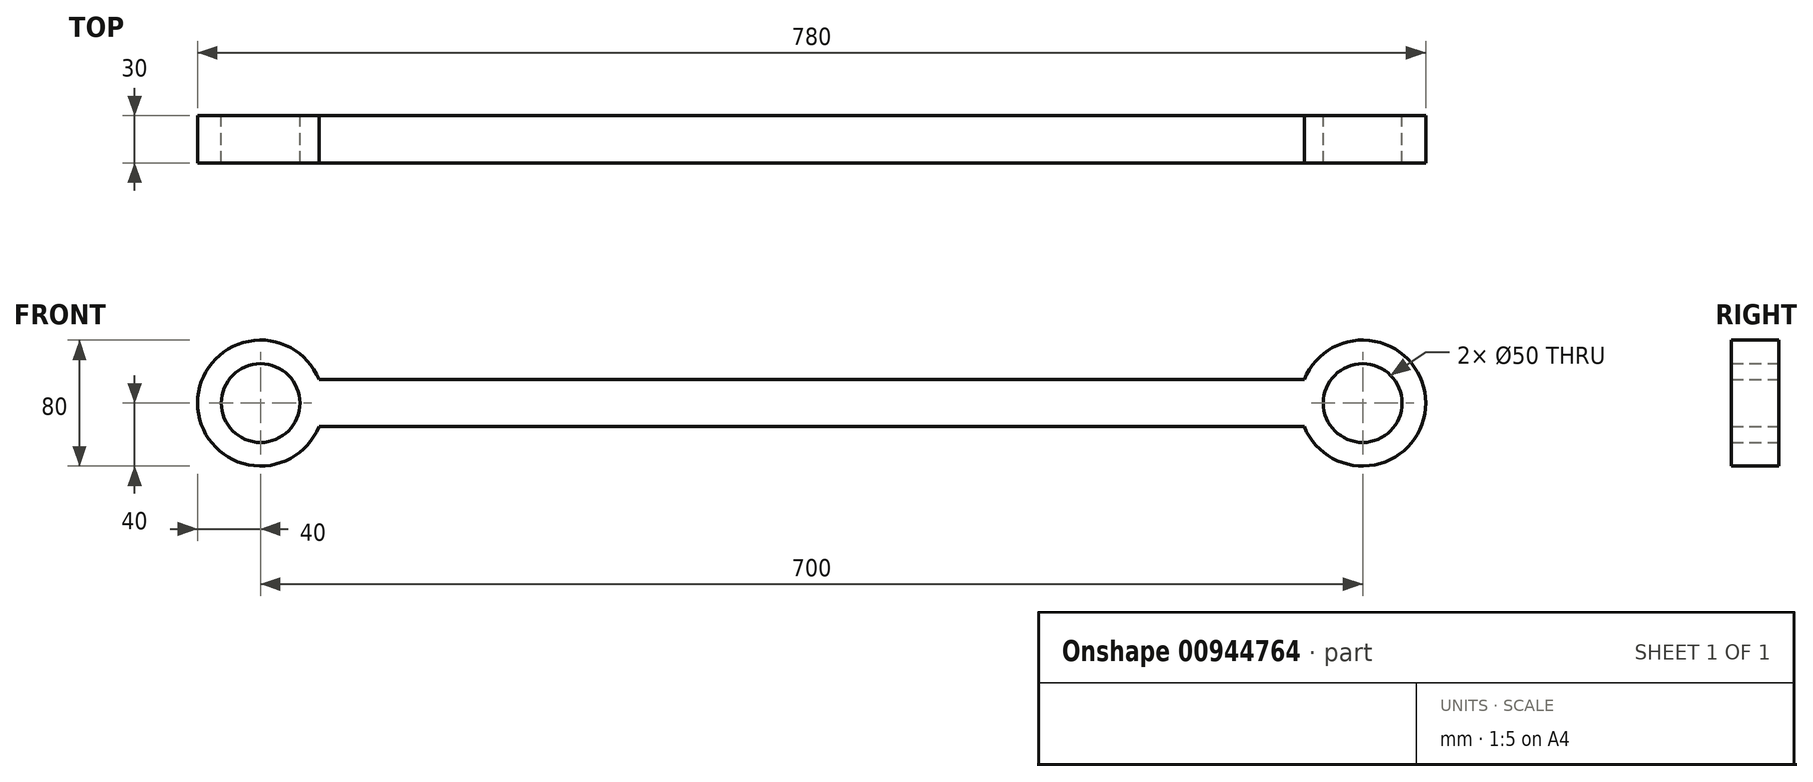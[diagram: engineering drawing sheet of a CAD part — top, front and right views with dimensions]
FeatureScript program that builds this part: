
annotation { "Feature Type Name" : "Feature", "Feature Type Description" : "" }
export const myFeature = defineFeature(function(context is Context, id is Id, definition is map)
    precondition{}
    {
        {
            var Q0;
            Q0=qCreatedBy(makeId("Front.planeOp"),FACE);
            var sketch = newSketch(context, id + "F0", { "sketchPlane" : qUnion([Q0])});
            skCircle(sketch, "E0", {"center": v(-350, 0) * mm, "radius": 25 * mm});
            skCircle(sketch, "E1", {"center": v(350, 0) * mm, "radius": 25 * mm});
            skArc(sketch, "E2", {"start": v(-312.92, 15) * mm, "mid": v(-390, 0) * mm, "end": v(-312.92, -15) * mm});
            skArc(sketch, "E3", {"start": v(312.92, -15) * mm, "mid": v(390, 0) * mm, "end": v(312.92, 15) * mm});
            skLineSegment(sketch, "E4.bottom", {"start": v(312.92, -15) * mm, "end": v(-312.92, -15) * mm});
            skLineSegment(sketch, "E4.top", {"start": v(312.92, 15) * mm, "end": v(-312.92, 15) * mm});
            skLineSegment(sketch, "E4.left", {"start": v(312.92, -15) * mm, "end": v(312.92, 15) * mm, "construction": true});
            skLineSegment(sketch, "E4.right", {"start": v(-312.92, -15) * mm, "end": v(-312.92, 15) * mm, "construction": true});
            skPoint(sketch, "E4.middle", {"position": v(0, 0) * mm});
            skLineSegment(sketch, "E5", {"start": v(-250.43, 0) * mm, "end": v(205.1, 0) * mm, "construction": true});
            skSolve(sketch);
        }
        {
            var Q0;
            Q0=qSketchRegion(id+"F0",true);
            extrude(context, id + "F1", {"entities" : qUnion([Q0]), "endBound" : BoundingType.SYMMETRIC, "depth" : 30 * mm, "offsetDistance" : 25 * mm});
        }
    });
